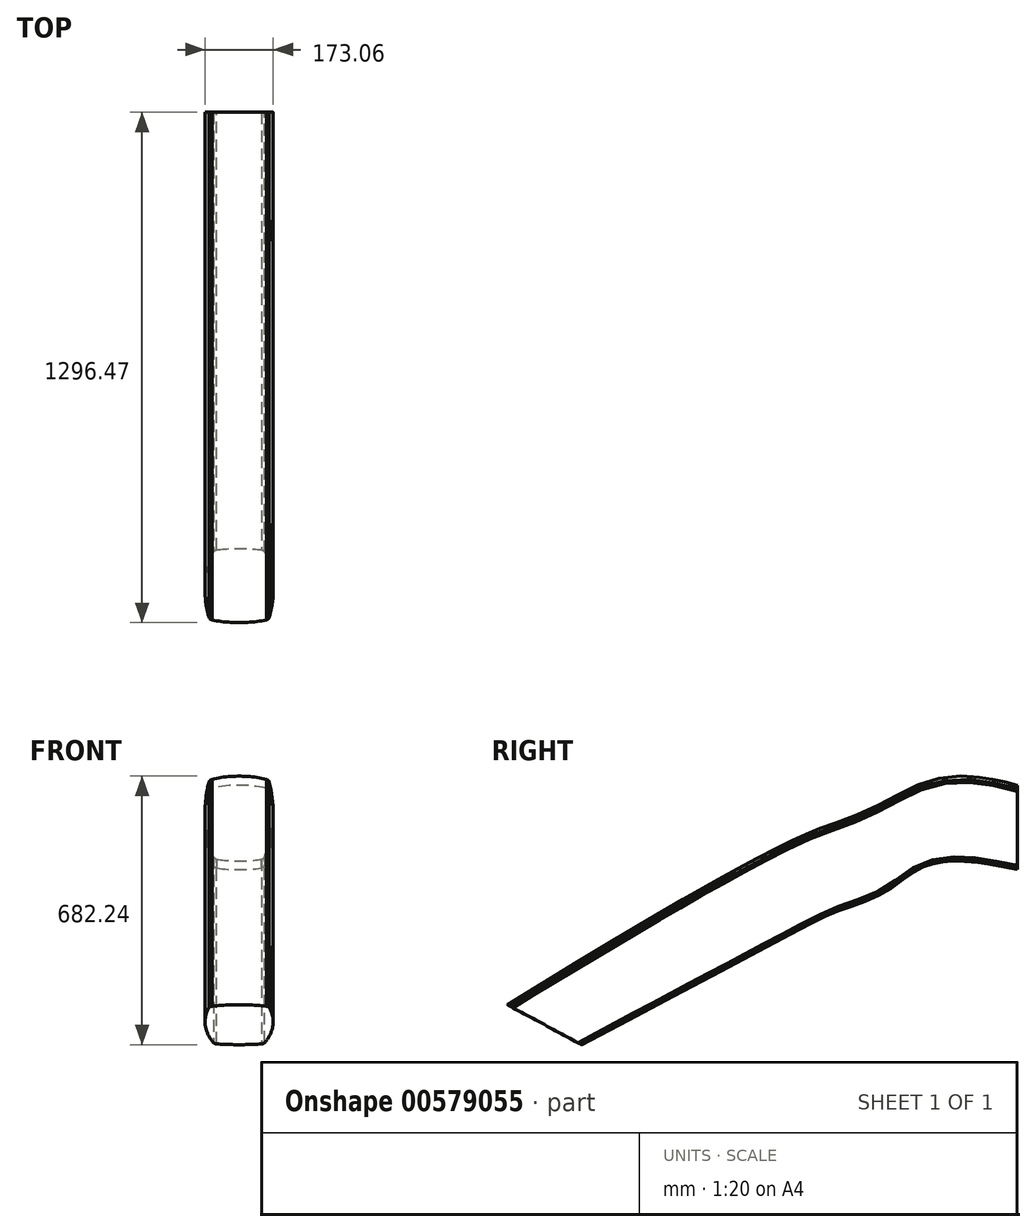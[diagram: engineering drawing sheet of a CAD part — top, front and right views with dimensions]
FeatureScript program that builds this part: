
annotation { "Feature Type Name" : "Feature", "Feature Type Description" : "" }
export const myFeature = defineFeature(function(context is Context, id is Id, definition is map)
    precondition{}
    {
        {
            var Q0;
            Q0=qCreatedBy(makeId("Right.planeOp"),FACE);
            var sketch = newSketch(context, id + "F0", { "sketchPlane" : qUnion([Q0])});
            skLineSegment(sketch, "E0", {"start": v(584.16, 0) * mm, "end": v(-1032.84, 0) * mm, "construction": true});
            skFitSpline(sketch, "E1", {"points": [v(0, 0) * mm, v(-200, -25) * mm, v(-350, -45) * mm, v(-500, -75) * mm, v(-600, -100) * mm, v(-800, -160) * mm, v(-1050, -300) * mm, v(-1200, -500) * mm], "startDerivative": vector(-1025.11, -4) * mm, "endDerivative": vector(-234.82, -436.8) * mm});
            skSolve(sketch);
        }
        {
            var Q0;
            Q0=qCreatedBy(makeId("Front.planeOp"),FACE);
            cPlane(context, id + "F1", {"entities" : qUnion([Q0]), "cplaneType" : CPlaneType.OFFSET, "offset" : (10 * 25.4) * mm, "width" : 150 * mm, "height" : 150 * mm});
        }
        {
            var Q0;
            Q0=sQuery(id+"F0.wireOp",EDGE,"E1");
            var Q1;
            Q1=sQuery(id+"F0.wireOp",VERTEX,"E1.2.internal");
            cPlane(context, id + "F2", {"entities" : qUnion([Q0, Q1]), "cplaneType" : CPlaneType.CURVE_POINT, "offset" : 25 * mm, "width" : 150 * mm, "height" : 150 * mm});
        }
        {
            var Q0;
            Q0=sQuery(id+"F0.wireOp",VERTEX,"E1.7.internal");
            var Q1;
            Q1=sQuery(id+"F0.wireOp",EDGE,"E1");
            cPlane(context, id + "F3", {"entities" : qUnion([Q0, Q1]), "cplaneType" : CPlaneType.CURVE_POINT, "offset" : 25 * mm, "width" : 150 * mm, "height" : 150 * mm});
        }
        {
            var Q0;
            Q0=sQuery(id+"F0.wireOp",EDGE,"E1");
            var Q1;
            Q1=sQuery(id+"F0.wireOp",VERTEX,"E1.3.internal");
            cPlane(context, id + "F4", {"entities" : qUnion([Q0, Q1]), "cplaneType" : CPlaneType.CURVE_POINT, "offset" : 25 * mm, "width" : 150 * mm, "height" : 150 * mm});
        }
        {
            var Q0;
            Q0=sQuery(id+"F0.wireOp",EDGE,"E1");
            var Q1;
            Q1=sQuery(id+"F0.wireOp",VERTEX,"E1.4.internal");
            cPlane(context, id + "F5", {"entities" : qUnion([Q0, Q1]), "cplaneType" : CPlaneType.CURVE_POINT, "offset" : 25 * mm, "width" : 150 * mm, "height" : 150 * mm});
        }
        {
            var Q0;
            Q0=qCreatedBy(makeId("Front.planeOp"),FACE);
            var sketch = newSketch(context, id + "F6", { "sketchPlane" : qUnion([Q0])});
            skLineSegment(sketch, "E2", {"start": v(-134.22, 0) * mm, "end": v(134.22, 0) * mm, "construction": true});
            skLineSegment(sketch, "E3", {"start": v(0, 92.73) * mm, "end": v(0, -92.73) * mm, "construction": true});
            skArc(sketch, "E4", {"start": v(-75, 100) * mm, "mid": v(-85.94, -1.07) * mm, "end": v(-62.5, -100) * mm});
            skArc(sketch, "E5", {"start": v(62.5, -100) * mm, "mid": v(85.94, -1.07) * mm, "end": v(75, 100) * mm});
            skArc(sketch, "E6", {"start": v(75, 100) * mm, "mid": v(0, 109.53) * mm, "end": v(-75, 100) * mm});
            skArc(sketch, "E7", {"start": v(-62.5, -100) * mm, "mid": v(0, -104.91) * mm, "end": v(62.5, -100) * mm});
            skSolve(sketch);
        }
        {
            var Q0;
            Q0=qCreatedBy(id+"F1.planeOp",FACE);
            var sketch = newSketch(context, id + "F7", { "sketchPlane" : qUnion([Q0])});
            skLineSegment(sketch, "E8", {"start": v(-134.22, 0) * mm, "end": v(134.22, 0) * mm, "construction": true});
            skLineSegment(sketch, "E9", {"start": v(0, 93) * mm, "end": v(0, -93) * mm, "construction": true});
            skArc(sketch, "E10", {"start": v(-75, 100) * mm, "mid": v(-85.94, -1.07) * mm, "end": v(-62.5, -100) * mm});
            skArc(sketch, "E11", {"start": v(62.5, -100) * mm, "mid": v(85.94, -1.07) * mm, "end": v(75, 100) * mm});
            skArc(sketch, "E12", {"start": v(75, 100) * mm, "mid": v(0, 109.53) * mm, "end": v(-75, 100) * mm});
            skArc(sketch, "E13", {"start": v(-62.5, -100) * mm, "mid": v(0, -104.91) * mm, "end": v(62.5, -100) * mm});
            skLineSegment(sketch, "E14", {"start": v(-219.7, 0) * mm, "end": v(219.7, 0) * mm, "construction": true});
            skPoint(sketch, "E15", {"position": v(0, 0) * mm});
            skSolve(sketch);
        }
        {
            var Q0;
            Q0=qCreatedBy(id+"F3.planeOp",FACE);
            var sketch = newSketch(context, id + "F8", { "sketchPlane" : qUnion([Q0])});
            skLineSegment(sketch, "E16", {"start": v(-134.22, 820.19) * mm, "end": v(134.22, 820.19) * mm, "construction": true});
            skLineSegment(sketch, "E17", {"start": v(0, 912.92) * mm, "end": v(0, 727.46) * mm, "construction": true});
            skArc(sketch, "E18", {"start": v(-75, 920.19) * mm, "mid": v(-85.94, 819.11) * mm, "end": v(-62.5, 720.19) * mm});
            skArc(sketch, "E19", {"start": v(62.5, 720.19) * mm, "mid": v(85.94, 819.11) * mm, "end": v(75, 920.19) * mm});
            skArc(sketch, "E20", {"start": v(75, 920.19) * mm, "mid": v(0, 929.71) * mm, "end": v(-75, 920.19) * mm});
            skArc(sketch, "E21", {"start": v(-62.5, 720.19) * mm, "mid": v(0, 715.28) * mm, "end": v(62.5, 720.19) * mm});
            skPoint(sketch, "E22", {"position": v(0, 820.19) * mm});
            skSolve(sketch);
        }
        {
            var Q0;
            Q0=qCreatedBy(id+"F2.planeOp",FACE);
            var sketch = newSketch(context, id + "F9", { "sketchPlane" : qUnion([Q0])});
            skLineSegment(sketch, "E23", {"start": v(-134.22, 0) * mm, "end": v(134.22, 0) * mm, "construction": true});
            skLineSegment(sketch, "E24", {"start": v(0, 321.85) * mm, "end": v(0, 136.4) * mm, "construction": true});
            skArc(sketch, "E25", {"start": v(-75, 100) * mm, "mid": v(-85.94, -1.07) * mm, "end": v(-62.5, -100) * mm});
            skArc(sketch, "E26", {"start": v(62.5, -100) * mm, "mid": v(85.94, -1.07) * mm, "end": v(75, 100) * mm});
            skArc(sketch, "E27", {"start": v(75, 100) * mm, "mid": v(0, 109.53) * mm, "end": v(-75, 100) * mm});
            skArc(sketch, "E28", {"start": v(-62.5, -100) * mm, "mid": v(0, -104.91) * mm, "end": v(62.5, -100) * mm});
            skSolve(sketch);
        }
        {
            var Q0;
            Q0=qCreatedBy(id+"F4.planeOp",FACE);
            var sketch = newSketch(context, id + "F10", { "sketchPlane" : qUnion([Q0])});
            skLineSegment(sketch, "E29", {"start": v(-134.22, 0) * mm, "end": v(134.22, 0) * mm, "construction": true});
            skLineSegment(sketch, "E30", {"start": v(0, -11.18) * mm, "end": v(0, -196.64) * mm, "construction": true});
            skArc(sketch, "E31", {"start": v(-75, 100) * mm, "mid": v(-85.94, -1.07) * mm, "end": v(-62.5, -100) * mm});
            skArc(sketch, "E32", {"start": v(62.5, -100) * mm, "mid": v(85.94, -1.07) * mm, "end": v(75, 100) * mm});
            skArc(sketch, "E33", {"start": v(75, 100) * mm, "mid": v(0, 109.53) * mm, "end": v(-75, 100) * mm});
            skArc(sketch, "E34", {"start": v(-62.5, -100) * mm, "mid": v(0, -104.91) * mm, "end": v(62.5, -100) * mm});
            skSolve(sketch);
        }
        {
            var Q0;
            Q0=qCreatedBy(id+"F5.planeOp",FACE);
            var sketch = newSketch(context, id + "F11", { "sketchPlane" : qUnion([Q0])});
            skLineSegment(sketch, "E35", {"start": v(-680.07, 0) * mm, "end": v(-411.62, 0) * mm, "construction": true});
            skLineSegment(sketch, "E36", {"start": v(0, 92.73) * mm, "end": v(0, -92.73) * mm, "construction": true});
            skArc(sketch, "E37", {"start": v(-75, 100) * mm, "mid": v(-85.94, -1.07) * mm, "end": v(-62.5, -100) * mm});
            skArc(sketch, "E38", {"start": v(62.5, -100) * mm, "mid": v(85.94, -1.07) * mm, "end": v(75, 100) * mm});
            skArc(sketch, "E39", {"start": v(75, 100) * mm, "mid": v(0, 109.53) * mm, "end": v(-75, 100) * mm});
            skArc(sketch, "E40", {"start": v(-62.5, -100) * mm, "mid": v(0, -104.91) * mm, "end": v(62.5, -100) * mm});
            skSolve(sketch);
        }
        {
            var Q0;
            Q0 = qSketchRegion(id + "F6", true);
            var Q1;
            Q1=makeQuery(id+"F7.imprint","IMPRINT",FACE,{"disambiguationData":[TD([[makeQuery(id+"F7.imprint","IMPRINT",EDGE,{"derivedFrom":sQuery(id+"F7.wireOp",EDGE,"E10")}),1.0]])]});
            var Q2;
            Q2=makeQuery(id+"F9.imprint","IMPRINT",FACE,{"disambiguationData":[TD([[makeQuery(id+"F9.imprint","IMPRINT",EDGE,{"derivedFrom":sQuery(id+"F9.wireOp",EDGE,"E25")}),1.0]])]});
            var Q3;
            Q3=makeQuery(id+"F10.imprint","IMPRINT",FACE,{"disambiguationData":[TD([[makeQuery(id+"F10.imprint","IMPRINT",EDGE,{"derivedFrom":sQuery(id+"F10.wireOp",EDGE,"E31")}),1.0]])]});
            var Q4;
            Q4=makeQuery(id+"F11.imprint","IMPRINT",FACE,{"disambiguationData":[TD([[makeQuery(id+"F11.imprint","IMPRINT",EDGE,{"derivedFrom":sQuery(id+"F11.wireOp",EDGE,"E37")}),1.0]])]});
            var Q5;
            Q5=makeQuery(id+"F8.imprint","IMPRINT",FACE,{"disambiguationData":[TD([[makeQuery(id+"F8.imprint","IMPRINT",EDGE,{"derivedFrom":sQuery(id+"F8.wireOp",EDGE,"E18")}),1.0]])]});
            var Q6;
            Q6=sQuery(id+"F7.wireOp",VERTEX,"E12.end");
            loft(context, id + "F12", {"sheetProfilesArray" : [{ "sheetProfileEntities" : qUnion([Q0]) }, { "sheetProfileEntities" : qUnion([Q1]) }, { "sheetProfileEntities" : qUnion([Q2]) }, { "sheetProfileEntities" : qUnion([Q3]) }, { "sheetProfileEntities" : qUnion([Q4]) }, { "sheetProfileEntities" : qUnion([Q5]) }], "connections" : [{ "connectionEntities" : qUnion([Q6]), "connectionEdgeQueries" : qUnion([]), "connectionEdgeParameters" : [] }]});
        }
        {
            var Q0;
            Q0=makeQuery(id+"F12.opLoft","SWEPT_EDGE",EDGE,{"disambiguationData":[OSD([sQuery(id+"F7.wireOp",EDGE,"E11"),sQuery(id+"F7.wireOp",EDGE,"E12"),sQuery(id+"F8.wireOp",EDGE,"E19"),sQuery(id+"F8.wireOp",EDGE,"E20")])]});
            var Q1;
            Q1=makeQuery(id+"F12.opLoft","SWEPT_EDGE",EDGE,{"disambiguationData":[OSD([sQuery(id+"F6.wireOp",EDGE,"E5"),sQuery(id+"F6.wireOp",EDGE,"E6"),sQuery(id+"F7.wireOp",EDGE,"E11"),sQuery(id+"F7.wireOp",EDGE,"E12")])]});
            var Q2;
            Q2=makeQuery(id+"F12.opLoft","SWEPT_EDGE",EDGE,{"disambiguationData":[OSD([sQuery(id+"F7.wireOp",EDGE,"E11"),sQuery(id+"F7.wireOp",EDGE,"E13"),sQuery(id+"F8.wireOp",EDGE,"E19"),sQuery(id+"F8.wireOp",EDGE,"E21")])]});
            var Q3;
            Q3=makeQuery(id+"F12.opLoft","SWEPT_EDGE",EDGE,{"disambiguationData":[OSD([sQuery(id+"F7.wireOp",EDGE,"E10"),sQuery(id+"F7.wireOp",EDGE,"E12"),sQuery(id+"F8.wireOp",EDGE,"E18"),sQuery(id+"F8.wireOp",EDGE,"E20")])]});
            var Q4;
            Q4=makeQuery(id+"F12.opLoft","SWEPT_EDGE",EDGE,{"disambiguationData":[OSD([sQuery(id+"F6.wireOp",EDGE,"E4"),sQuery(id+"F6.wireOp",EDGE,"E7"),sQuery(id+"F7.wireOp",EDGE,"E10"),sQuery(id+"F7.wireOp",EDGE,"E13")])]});
            fillet(context, id + "F13", {"entities" : qUnion([Q0, Q1, Q2, Q3, Q4]), "radius" : 10 * mm, "tangentPropagation" : true, "allowEdgeOverflow" : false});
        }
    });
